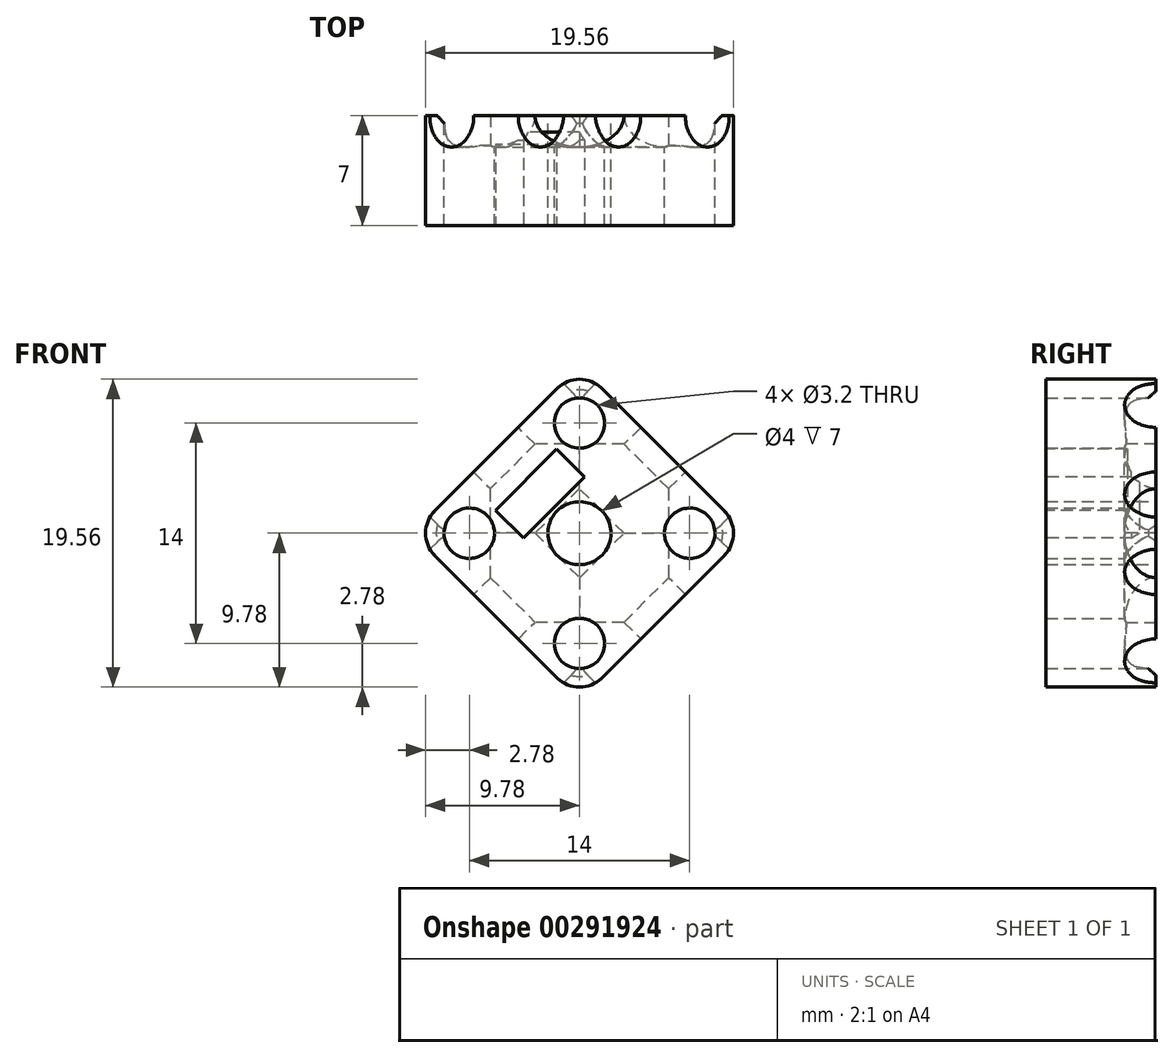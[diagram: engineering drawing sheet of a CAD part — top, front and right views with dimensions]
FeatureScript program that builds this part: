
annotation { "Feature Type Name" : "Feature", "Feature Type Description" : "" }
export const myFeature = defineFeature(function(context is Context, id is Id, definition is map)
    precondition{}
    {
        {
            var Q0;
            Q0=qCreatedBy(makeId("Front.planeOp"),FACE);
            var sketch = newSketch(context, id + "F0", { "sketchPlane" : qUnion([Q0])});
            skLineSegment(sketch, "E0.bottom", {"start": v(-1.41, -9.2) * mm, "end": v(-9.2, -1.41) * mm});
            skLineSegment(sketch, "E0.top", {"start": v(9.2, 1.41) * mm, "end": v(1.41, 9.2) * mm});
            skLineSegment(sketch, "E0.left", {"start": v(1.41, -9.2) * mm, "end": v(9.2, -1.41) * mm});
            skLineSegment(sketch, "E0.right", {"start": v(-9.2, 1.41) * mm, "end": v(-1.41, 9.2) * mm});
            skCircle(sketch, "E1", {"center": v(0, 7) * mm, "radius": 1.6 * mm});
            skCircle(sketch, "E2", {"center": v(0, 0) * mm, "radius": 2 * mm});
            skCircle(sketch, "E3.1.1", {"center": v(-7, 0) * mm, "radius": 1.6 * mm});
            skCircle(sketch, "E3.2.1", {"center": v(0, -7) * mm, "radius": 1.6 * mm});
            skCircle(sketch, "E3.3.1", {"center": v(7, 0) * mm, "radius": 1.6 * mm});
            skPoint(sketch, "E4.visualSharp", {"position": v(-10.6, 0) * mm});
            skArc(sketch, "E4.filletArc", {"start": v(-9.2, 1.41) * mm, "mid": v(-9.78, 0) * mm, "end": v(-9.2, -1.41) * mm});
            skPoint(sketch, "E5.visualSharp", {"position": v(0, -10.6) * mm});
            skArc(sketch, "E5.filletArc", {"start": v(-1.41, -9.2) * mm, "mid": v(0, -9.78) * mm, "end": v(1.41, -9.2) * mm});
            skPoint(sketch, "E6.visualSharp", {"position": v(10.6, 0) * mm});
            skArc(sketch, "E6.filletArc", {"start": v(9.2, -1.41) * mm, "mid": v(9.78, 0) * mm, "end": v(9.2, 1.41) * mm});
            skPoint(sketch, "E7.visualSharp", {"position": v(0, 10.6) * mm});
            skArc(sketch, "E7.filletArc", {"start": v(1.41, 9.2) * mm, "mid": v(0, 9.78) * mm, "end": v(-1.41, 9.2) * mm});
            skSolve(sketch);
        }
        {
            var Q0;
            Q0=makeQuery(id+"F0.imprint","IMPRINT",FACE,{"disambiguationData":[TD([[makeQuery(id+"F0.imprint","IMPRINT",EDGE,{"derivedFrom":sQuery(id+"F0.wireOp",EDGE,"E0.bottom")}),-1.0]])]});
            extrude(context, id + "F1", {"entities" : qUnion([Q0]), "depth" : 7 * mm});
        }
        {
            var Q0;
            Q0=makeQuery(id+"F1.opExtrude","SWEPT_FACE",FACE,{"disambiguationData":[OSD([sQuery(id+"F0.wireOp",EDGE,"E0.bottom")])]});
            var sketch = newSketch(context, id + "F2", { "sketchPlane" : qUnion([Q0])});
            skCircle(sketch, "E8", {"center": v(0, 4) * mm, "radius": 2 * mm});
            skSolve(sketch);
        }
        {
            var Q0;
            Q0=makeQuery(id+"F2.imprint","IMPRINT",FACE,{"disambiguationData":[TD([[makeQuery(id+"F2.imprint","IMPRINT",EDGE,{"derivedFrom":sQuery(id+"F2.wireOp",EDGE,"E8")}),1.0]])]});
            extrude(context, id + "F3", {"entities" : qUnion([Q0]), "oppositeDirection" : true, "depth" : 25 * mm});
        }
        {
            var Q0;
            Q0=makeQuery(id+"F3.opExtrude","SWEPT_BODY",BODY,{"disambiguationData":[OSD([sQuery(id+"F2.wireOp",EDGE,"E8")])]});
            var Q1;
            Q1=makeQuery(id+"F1.opExtrude","SWEPT_FACE",FACE,{"disambiguationData":[OSD([sQuery(id+"F0.wireOp",EDGE,"E2")])]});
            circularPattern(context, id + "F4", {"entities" : qUnion([Q0]), "axis" : qUnion([Q1]), "angle" : 360 * degree, "instanceCount" : 4, "equalSpace" : true});
        }
        {
            var Q0;
            Q0=makeQuery(id+"F3.opExtrude","SWEPT_BODY",BODY,{"disambiguationData":[OSD([sQuery(id+"F2.wireOp",EDGE,"E8")])]});
            var Q1;
            Q1=makeQuery(id+"F4.opPattern","COPY",BODY,{"derivedFrom":makeQuery(id+"F3.opExtrude","SWEPT_BODY",BODY,{"disambiguationData":[OSD([sQuery(id+"F2.wireOp",EDGE,"E8")])]}),"instanceName":"1"});
            var Q2;
            Q2=makeQuery(id+"F4.opPattern","COPY",BODY,{"derivedFrom":makeQuery(id+"F3.opExtrude","SWEPT_BODY",BODY,{"disambiguationData":[OSD([sQuery(id+"F2.wireOp",EDGE,"E8")])]}),"instanceName":"2"});
            var Q3;
            Q3=makeQuery(id+"F4.opPattern","COPY",BODY,{"derivedFrom":makeQuery(id+"F3.opExtrude","SWEPT_BODY",BODY,{"disambiguationData":[OSD([sQuery(id+"F2.wireOp",EDGE,"E8")])]}),"instanceName":"3"});
            var Q4;
            Q4=makeQuery(id+"F1.opExtrude","SWEPT_BODY",BODY,{"disambiguationData":[OSD([sQuery(id+"F0.wireOp",EDGE,"E0.bottom"),sQuery(id+"F0.wireOp",EDGE,"E0.top"),sQuery(id+"F0.wireOp",EDGE,"E0.left"),sQuery(id+"F0.wireOp",EDGE,"E0.right"),sQuery(id+"F0.wireOp",EDGE,"E1"),sQuery(id+"F0.wireOp",EDGE,"E3.1.1"),sQuery(id+"F0.wireOp",EDGE,"E3.2.1"),sQuery(id+"F0.wireOp",EDGE,"E2"),sQuery(id+"F0.wireOp",EDGE,"E3.3.1"),sQuery(id+"F0.wireOp",EDGE,"E4.filletArc"),sQuery(id+"F0.wireOp",EDGE,"E5.filletArc"),sQuery(id+"F0.wireOp",EDGE,"E6.filletArc"),sQuery(id+"F0.wireOp",EDGE,"E7.filletArc")])]});
            booleanBodies(context, id + "F5", {"operationType" : BooleanOperationType.SUBTRACTION, "tools" : qUnion([Q0, Q1, Q2, Q3]), "targets" : qUnion([Q4])});
        }
        {
            var Q0;
            Q0=makeQuery(id+"F1.opExtrude","CAP_FACE",FACE,{"disambiguationData":[OSD([sQuery(id+"F0.wireOp",EDGE,"E0.bottom"),sQuery(id+"F0.wireOp",EDGE,"E0.top"),sQuery(id+"F0.wireOp",EDGE,"E0.left"),sQuery(id+"F0.wireOp",EDGE,"E0.right"),sQuery(id+"F0.wireOp",EDGE,"E1"),sQuery(id+"F0.wireOp",EDGE,"E3.1.1"),sQuery(id+"F0.wireOp",EDGE,"E3.2.1"),sQuery(id+"F0.wireOp",EDGE,"E2"),sQuery(id+"F0.wireOp",EDGE,"E3.3.1"),sQuery(id+"F0.wireOp",EDGE,"E4.filletArc"),sQuery(id+"F0.wireOp",EDGE,"E5.filletArc"),sQuery(id+"F0.wireOp",EDGE,"E6.filletArc"),sQuery(id+"F0.wireOp",EDGE,"E7.filletArc")])],"isStart":false});
            var sketch = newSketch(context, id + "F6", { "sketchPlane" : qUnion([Q0])});
            skLineSegment(sketch, "E9", {"start": v(0, 0) * mm, "end": v(-5.3, 5.3) * mm, "construction": true});
            skLineSegment(sketch, "E10", {"start": v(-3.4, 3.4) * mm, "end": v(-1.45, 5.34) * mm});
            skLineSegment(sketch, "E11", {"start": v(-1.45, 5.34) * mm, "end": v(0.32, 3.57) * mm});
            skLineSegment(sketch, "E12", {"start": v(0.32, 3.57) * mm, "end": v(-3.57, -0.32) * mm});
            skLineSegment(sketch, "E13", {"start": v(-3.57, -0.32) * mm, "end": v(-5.34, 1.45) * mm});
            skLineSegment(sketch, "E14", {"start": v(-5.34, 1.45) * mm, "end": v(-3.4, 3.4) * mm});
            skSolve(sketch);
        }
        {
            var Q0;
            Q0=makeQuery(id+"F6.imprint","IMPRINT",FACE,{"disambiguationData":[TD([[makeQuery(id+"F6.imprint","IMPRINT",EDGE,{"derivedFrom":sQuery(id+"F6.wireOp",EDGE,"E10")}),-1.0]])]});
            extrude(context, id + "F7", {"entities" : qUnion([Q0]), "operationType" : NewBodyOperationType.REMOVE, "oppositeDirection" : true, "depth" : 6 * mm, "offsetDistance" : 25 * mm});
        }
        {
            var Q0;
            Q0=makeQuery(id+"F1.opExtrude","CAP_EDGE",EDGE,{"disambiguationData":[OSD([sQuery(id+"F0.wireOp",EDGE,"E3.3.1")])],"isStart":true});
            var Q1;
            Q1=makeQuery(id+"F1.opExtrude","CAP_EDGE",EDGE,{"disambiguationData":[OSD([sQuery(id+"F0.wireOp",EDGE,"E1")])],"isStart":true});
            var Q2;
            Q2=makeQuery(id+"F1.opExtrude","CAP_EDGE",EDGE,{"disambiguationData":[OSD([sQuery(id+"F0.wireOp",EDGE,"E3.1.1")])],"isStart":true});
            var Q3;
            Q3=makeQuery(id+"F1.opExtrude","CAP_EDGE",EDGE,{"disambiguationData":[OSD([sQuery(id+"F0.wireOp",EDGE,"E3.2.1")])],"isStart":true});
            chamfer(context, id + "F8", {"entities" : qUnion([Q0, Q1, Q2, Q3]), "width" : 0.5 * mm, "tangentPropagation" : true});
        }
    });
